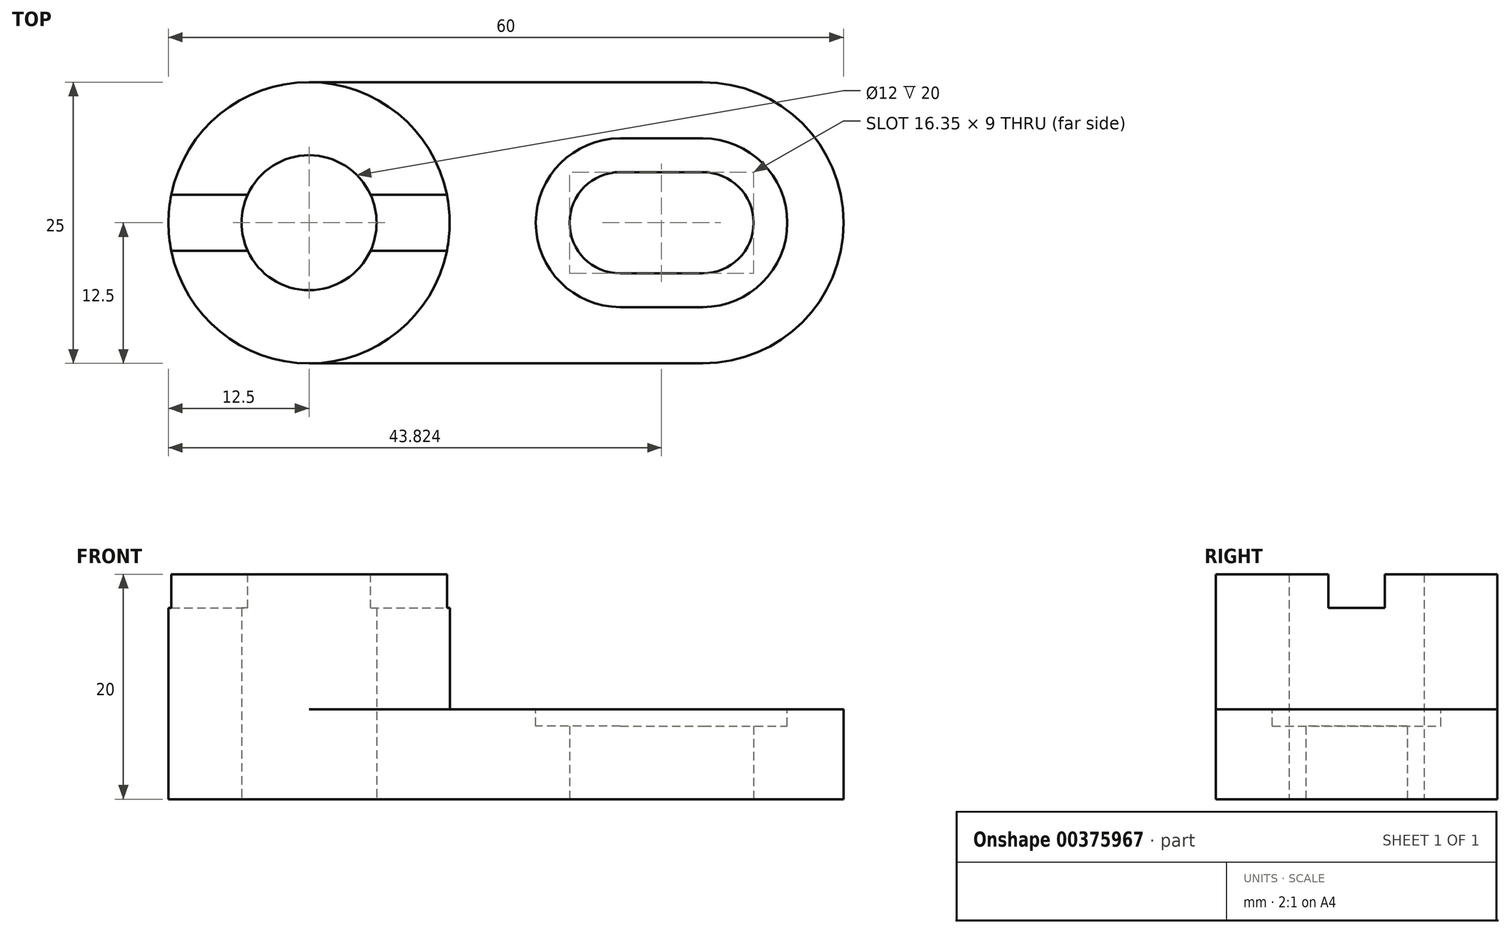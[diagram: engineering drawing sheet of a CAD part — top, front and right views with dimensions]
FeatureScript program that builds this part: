
annotation { "Feature Type Name" : "Feature", "Feature Type Description" : "" }
export const myFeature = defineFeature(function(context is Context, id is Id, definition is map)
    precondition{}
    {
        {
            var Q0;
            Q0=qCreatedBy(makeId("Top.planeOp"),FACE);
            var sketch = newSketch(context, id + "F0", { "sketchPlane" : qUnion([Q0])});
            skLineSegment(sketch, "E0.bottom", {"start": v(12.5, 0) * mm, "end": v(47.5, 0) * mm});
            skLineSegment(sketch, "E0.top", {"start": v(12.5, -25) * mm, "end": v(47.5, -25) * mm});
            skArc(sketch, "E1", {"start": v(12.5, 0) * mm, "mid": v(0, -12.5) * mm, "end": v(12.5, -25) * mm});
            skArc(sketch, "E2", {"start": v(47.5, -25) * mm, "mid": v(60, -12.5) * mm, "end": v(47.5, 0) * mm});
            skArc(sketch, "E3.0", {"start": v(47.5, -17) * mm, "mid": v(52, -12.5) * mm, "end": v(47.5, -8) * mm});
            skArc(sketch, "E4.MirrorCS", {"start": v(40.15, -17) * mm, "mid": v(35.65, -12.5) * mm, "end": v(40.15, -8) * mm});
            skLineSegment(sketch, "E5", {"start": v(40.15, -8) * mm, "end": v(47.5, -8) * mm});
            skLineSegment(sketch, "E6", {"start": v(40.15, -17) * mm, "end": v(47.5, -17) * mm});
            skCircle(sketch, "E7", {"center": v(12.5, -12.5) * mm, "radius": 6 * mm});
            skSolve(sketch);
        }
        {
            var Q0;
            Q0=makeQuery(id+"F0.imprint","IMPRINT",FACE,{"disambiguationData":[TD([[makeQuery(id+"F0.imprint","IMPRINT",EDGE,{"derivedFrom":sQuery(id+"F0.wireOp",EDGE,"E0.bottom")}),-1.0]])]});
            extrude(context, id + "F1", {"entities" : qUnion([Q0]), "depth" : 8 * mm});
        }
        {
            var Q0;
            Q0=makeQuery(id+"F1.opExtrude","CAP_FACE",FACE,{"disambiguationData":[OSD([sQuery(id+"F0.wireOp",EDGE,"E0.bottom"),sQuery(id+"F0.wireOp",EDGE,"E0.top"),sQuery(id+"F0.wireOp",EDGE,"E1"),sQuery(id+"F0.wireOp",EDGE,"E2"),sQuery(id+"F0.wireOp",EDGE,"E3.0"),sQuery(id+"F0.wireOp",EDGE,"E4.MirrorCS"),sQuery(id+"F0.wireOp",EDGE,"E5"),sQuery(id+"F0.wireOp",EDGE,"E6"),sQuery(id+"F0.wireOp",EDGE,"E7")])],"isStart":false});
            var sketch = newSketch(context, id + "F2", { "sketchPlane" : qUnion([Q0])});
            skArc(sketch, "E8.0", {"start": v(47.5, -20) * mm, "mid": v(55, -12.5) * mm, "end": v(47.5, -5) * mm});
            skLineSegment(sketch, "E8.1", {"start": v(40.15, -20) * mm, "end": v(47.5, -20) * mm});
            skArc(sketch, "E8.2", {"start": v(40.15, -20) * mm, "mid": v(32.65, -12.5) * mm, "end": v(40.15, -5) * mm});
            skLineSegment(sketch, "E8.3", {"start": v(40.15, -5) * mm, "end": v(47.5, -5) * mm});
            skSolve(sketch);
        }
        {
            var Q0;
            Q0=makeQuery(id+"F2.imprint","IMPRINT",FACE,{"disambiguationData":[TD([[makeQuery(id+"F2.imprint","IMPRINT",EDGE,{"derivedFrom":sQuery(id+"F2.wireOp",EDGE,"E8.0")}),1.0]])]});
            extrude(context, id + "F3", {"entities" : qUnion([Q0]), "operationType" : NewBodyOperationType.REMOVE, "oppositeDirection" : true, "depth" : 1.5 * mm});
        }
        {
            var Q0;
            Q0=makeQuery(id+"F1.opExtrude","CAP_FACE",FACE,{"disambiguationData":[OSD([sQuery(id+"F0.wireOp",EDGE,"E0.bottom"),sQuery(id+"F0.wireOp",EDGE,"E0.top"),sQuery(id+"F0.wireOp",EDGE,"E1"),sQuery(id+"F0.wireOp",EDGE,"E2"),sQuery(id+"F0.wireOp",EDGE,"E3.0"),sQuery(id+"F0.wireOp",EDGE,"E4.MirrorCS"),sQuery(id+"F0.wireOp",EDGE,"E5"),sQuery(id+"F0.wireOp",EDGE,"E6"),sQuery(id+"F0.wireOp",EDGE,"E7")])],"isStart":false});
            var sketch = newSketch(context, id + "F4", { "sketchPlane" : qUnion([Q0])});
            skCircle(sketch, "E9", {"center": v(12.5, -12.5) * mm, "radius": 12.5 * mm});
            skCircle(sketch, "E10", {"center": v(12.5, -12.5) * mm, "radius": 6 * mm});
            skSolve(sketch);
        }
        {
            var Q0;
            Q0=makeQuery(id+"F4.imprint","IMPRINT",FACE,{"disambiguationData":[TD([[makeQuery(id+"F4.imprint","IMPRINT",EDGE,{"derivedFrom":sQuery(id+"F4.wireOp",EDGE,"E10")}),-1.0]])]});
            extrude(context, id + "F5", {"entities" : qUnion([Q0]), "operationType" : NewBodyOperationType.ADD, "depth" : 12 * mm});
        }
        {
            var Q0;
            Q0=makeQuery(id+"F5.opExtrude","CAP_FACE",FACE,{"disambiguationData":[OSD([sQuery(id+"F4.wireOp",EDGE,"E9"),sQuery(id+"F4.wireOp",EDGE,"E10")])],"isStart":false});
            var sketch = newSketch(context, id + "F6", { "sketchPlane" : qUnion([Q0])});
            skPoint(sketch, "E11.orphan", {"position": v(12.5, -12.5) * mm});
            skLineSegment(sketch, "E12.0", {"start": v(0.25, -15) * mm, "end": v(7.05, -15) * mm});
            skLineSegment(sketch, "E13.MirrorCS", {"start": v(0.25, -10) * mm, "end": v(7.05, -10) * mm});
            skArc(sketch, "E14", {"start": v(0.25, -10) * mm, "mid": v(0, -12.5) * mm, "end": v(0.25, -15) * mm});
            skArc(sketch, "E15.trimOffspring", {"start": v(24.75, -15) * mm, "mid": v(25, -12.5) * mm, "end": v(24.75, -10) * mm});
            skArc(sketch, "E16", {"start": v(7.05, -10) * mm, "mid": v(6.5, -12.5) * mm, "end": v(7.05, -15) * mm});
            skArc(sketch, "E17.trimOffspring", {"start": v(17.95, -15) * mm, "mid": v(18.5, -12.5) * mm, "end": v(17.95, -10) * mm});
            skLineSegment(sketch, "E18.trimOffspring", {"start": v(17.95, -10) * mm, "end": v(24.75, -10) * mm});
            skLineSegment(sketch, "E19.trimOffspring", {"start": v(17.95, -15) * mm, "end": v(24.75, -15) * mm});
            skSolve(sketch);
        }
        {
            var Q0;
            Q0=makeQuery(id+"F6.imprint","IMPRINT",FACE,{"disambiguationData":[TD([[makeQuery(id+"F6.imprint","IMPRINT",EDGE,{"derivedFrom":sQuery(id+"F6.wireOp",EDGE,"E15.trimOffspring")}),1.0]])]});
            var Q1;
            Q1=makeQuery(id+"F6.imprint","IMPRINT",FACE,{"disambiguationData":[TD([[makeQuery(id+"F6.imprint","IMPRINT",EDGE,{"derivedFrom":sQuery(id+"F6.wireOp",EDGE,"E12.0")}),1.0]])]});
            extrude(context, id + "F7", {"entities" : qUnion([Q0, Q1]), "operationType" : NewBodyOperationType.REMOVE, "oppositeDirection" : true, "depth" : 3 * mm});
        }
    });
